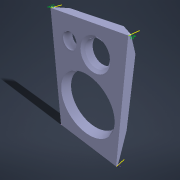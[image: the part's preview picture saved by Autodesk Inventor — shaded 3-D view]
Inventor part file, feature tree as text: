
AUTODESK INVENTOR PART (.ipt)
format: ipt  version: 2022 (Build 260153000, 153)  size: 200,192 bytes
history: native  units: mm
features: other x9, extrude x4, chamfer x3, sketch x2
ambient origin geometry x8: Origin, YZ Plane, XZ Plane, XY Plane, X Axis, Y Axis, Z Axis, Center Point
bodies: Body1 (feature_tree)
feature tree (18):
  other  "Твердое тело1"
  extrude  "Выдавливание1"  Depth=290.0mm
  sketch  "Эскиз3"
  sketch  "Эскиз4"
  chamfer  "Фаска2"  Distance=470.0mm
  chamfer  "Фаска3"  Distance=266.0mm
  other  "РабПлоскость8"
  other  "Разделение8"
  other  "РабПлоскость9"
  other  "Разделение9"
  other  "РабПлоскость10"
  other  "Разделение10"
  other  "РабПлоскость11"
  other  "Разделение11"
  chamfer  "Фаска5"  Distance=230.0mm
  extrude  "Выдавливание2"  Depth=94.0mm
  extrude  "Выдавливание3"  Depth=60.0mm
  extrude  "Выдавливание4"  Depth=94.0mm
